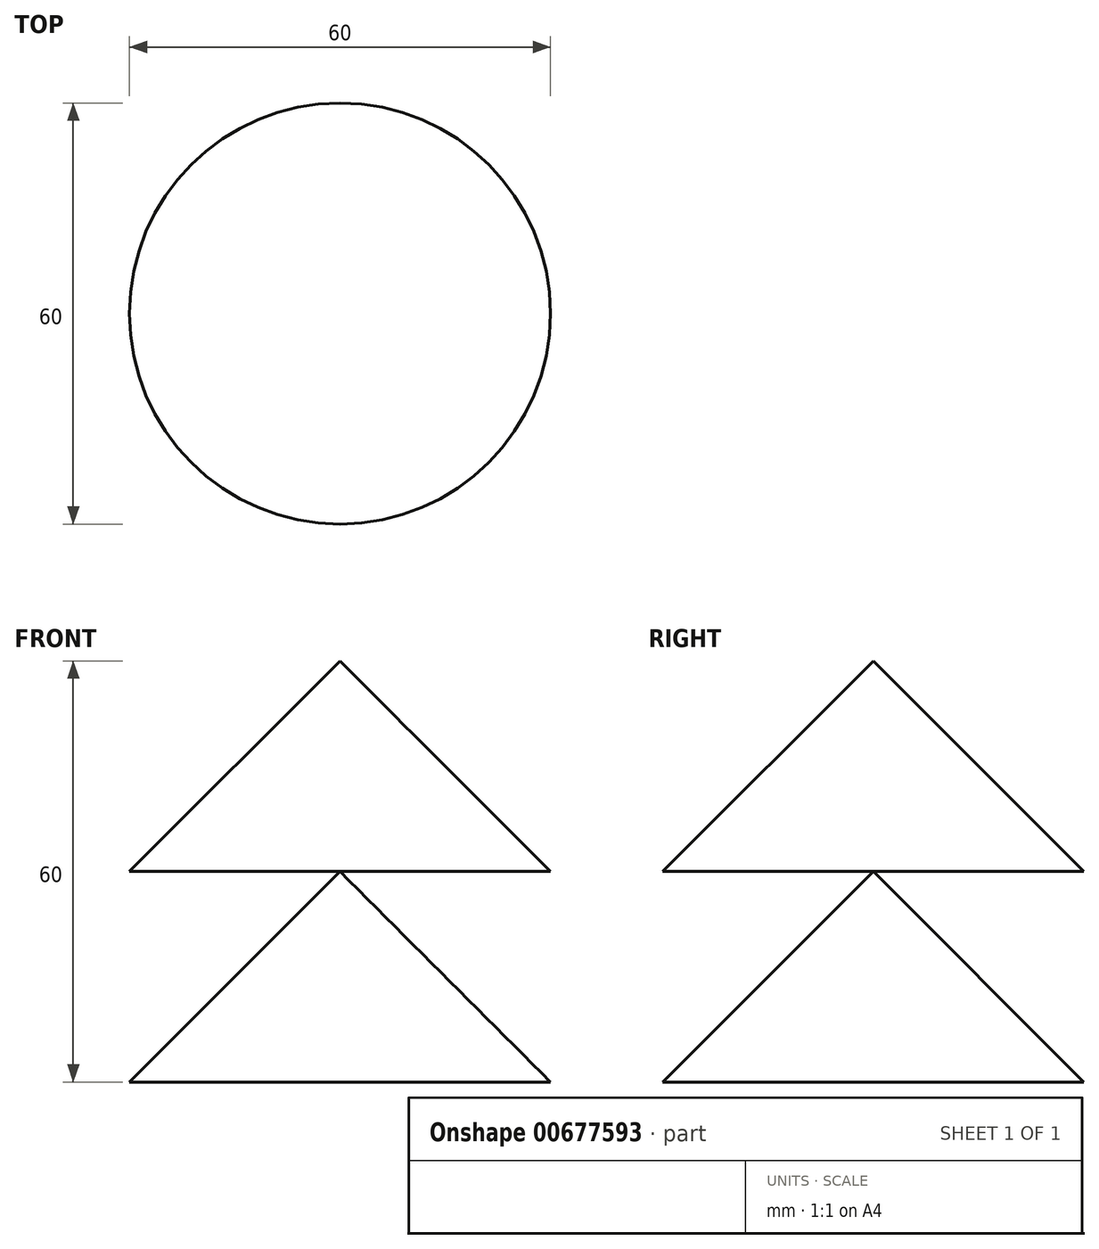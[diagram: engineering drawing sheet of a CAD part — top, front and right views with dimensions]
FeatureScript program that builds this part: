
annotation { "Feature Type Name" : "Feature", "Feature Type Description" : "" }
export const myFeature = defineFeature(function(context is Context, id is Id, definition is map)
    precondition{}
    {
        {
            var Q0;
            Q0=qCreatedBy(makeId("Top.planeOp"),FACE);
            var sketch = newSketch(context, id + "F0", { "sketchPlane" : qUnion([Q0])});
            skCircle(sketch, "E0", {"center": v(0, 0) * mm, "radius": 30 * mm});
            skSolve(sketch);
        }
        {
            var Q0;
            Q0 = qSketchRegion(id + "F0", true);
            extrude(context, id + "F1", {"entities" : qUnion([Q0]), "depth" : 30 * mm, "offsetDistance" : 25 * mm, "hasDraft" : true, "draftAngle" : 45 * degree, "draftPullDirection" : true});
        }
        {
            var Q0;
            Q0=qCreatedBy(makeId("Top.planeOp"),FACE);
            cPlane(context, id + "F2", {"entities" : qUnion([Q0]), "cplaneType" : CPlaneType.OFFSET, "offset" : 30 * mm, "width" : 150 * mm, "height" : 150 * mm});
        }
        {
            var Q0;
            Q0=qCreatedBy(id+"F2.planeOp",FACE);
            var sketch = newSketch(context, id + "F3", { "sketchPlane" : qUnion([Q0])});
            skCircle(sketch, "E1.0", {"center": v(0, 0) * mm, "radius": 30 * mm});
            skSolve(sketch);
        }
        {
            var Q0;
            Q0 = qSketchRegion(id + "F3", true);
            extrude(context, id + "F4", {"entities" : qUnion([Q0]), "operationType" : NewBodyOperationType.ADD, "depth" : 30 * mm, "offsetDistance" : 25 * mm, "hasDraft" : true, "draftAngle" : 45 * degree, "draftPullDirection" : true});
        }
    });
